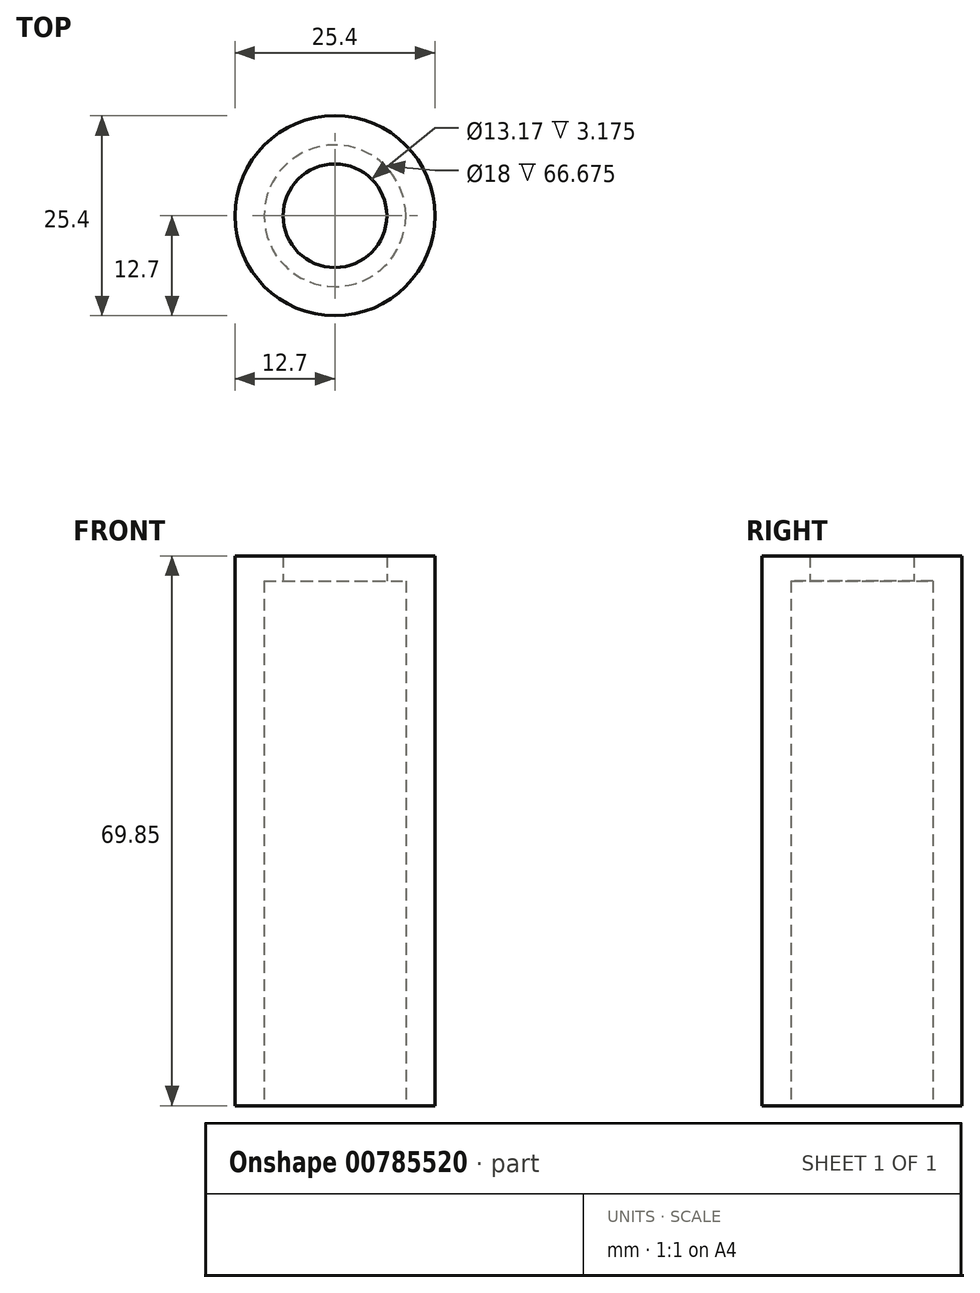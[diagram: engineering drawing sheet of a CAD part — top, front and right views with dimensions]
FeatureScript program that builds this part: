
annotation { "Feature Type Name" : "Feature", "Feature Type Description" : "" }
export const myFeature = defineFeature(function(context is Context, id is Id, definition is map)
    precondition{}
    {
        {
            var Q0;
            Q0=qCreatedBy(makeId("Front.planeOp"),FACE);
            var sketch = newSketch(context, id + "F0", { "sketchPlane" : qUnion([Q0])});
            skLineSegment(sketch, "E0", {"start": v(12.7, 69.85) * mm, "end": v(12.7, 0) * mm});
            skLineSegment(sketch, "E1", {"start": v(12.7, 69.85) * mm, "end": v(6.59, 69.85) * mm});
            skLineSegment(sketch, "E2", {"start": v(6.59, 69.85) * mm, "end": v(6.59, 66.68) * mm});
            skLineSegment(sketch, "E3", {"start": v(6.59, 66.68) * mm, "end": v(9, 66.68) * mm});
            skLineSegment(sketch, "E4", {"start": v(9, 66.68) * mm, "end": v(9, 0) * mm});
            skLineSegment(sketch, "E5", {"start": v(9, 0) * mm, "end": v(12.7, 0) * mm});
            skLineSegment(sketch, "E6", {"start": v(0, 0) * mm, "end": v(0, 69.85) * mm, "construction": true});
            skSolve(sketch);
        }
        {
            var Q0;
            Q0=makeQuery(id+"F0.imprint","IMPRINT",FACE,{"disambiguationData":[TD([[makeQuery(id+"F0.imprint","IMPRINT",EDGE,{"derivedFrom":sQuery(id+"F0.wireOp",EDGE,"E0")}),-1.0]])]});
            var Q1;
            Q1=sQuery(id+"F0.wireOp",EDGE,"E6");
            revolve(context, id + "F1", {"surfaceOperationType" : NewSurfaceOperationType.NEW, "entities" : qUnion([Q0]), "axis" : qUnion([Q1]), "revolveType" : RevolveType.FULL});
        }
    });
